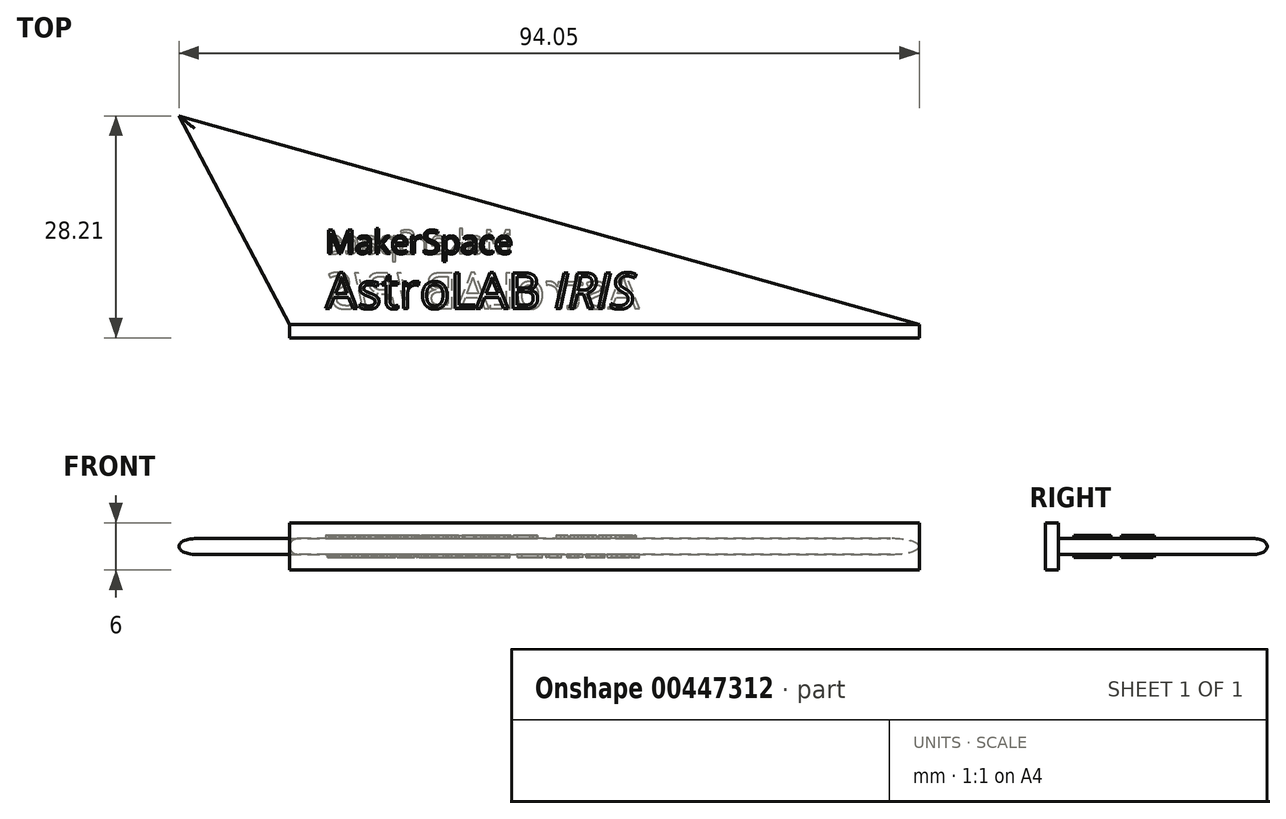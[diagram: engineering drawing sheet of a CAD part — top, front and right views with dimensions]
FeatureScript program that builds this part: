
annotation { "Feature Type Name" : "Feature", "Feature Type Description" : "" }
export const myFeature = defineFeature(function(context is Context, id is Id, definition is map)
    precondition{}
    {
        {
            var Q0;
            Q0=qCreatedBy(makeId("Front.planeOp"),FACE);
            var sketch = newSketch(context, id + "F0", { "sketchPlane" : qUnion([Q0])});
            skLineSegment(sketch, "E0.bottom", {"start": v(-40, 3) * mm, "end": v(40, 3) * mm});
            skLineSegment(sketch, "E0.top", {"start": v(-40, -3) * mm, "end": v(40, -3) * mm});
            skLineSegment(sketch, "E0.left", {"start": v(-40, 3) * mm, "end": v(-40, -3) * mm});
            skLineSegment(sketch, "E0.right", {"start": v(40, 3) * mm, "end": v(40, -3) * mm});
            skPoint(sketch, "E0.middle", {"position": v(0, 0) * mm});
            skSolve(sketch);
        }
        {
            var Q0;
            Q0=qCreatedBy(makeId("Front.planeOp"),FACE);
            var sketch = newSketch(context, id + "F1", { "sketchPlane" : qUnion([Q0])});
            skLineSegment(sketch, "E1.bottom", {"start": v(-40, 0.85) * mm, "end": v(40, 0.85) * mm});
            skLineSegment(sketch, "E1.top", {"start": v(-40, -0.85) * mm, "end": v(40, -0.85) * mm});
            skLineSegment(sketch, "E1.left", {"start": v(-40, 0.85) * mm, "end": v(-40, -0.85) * mm});
            skLineSegment(sketch, "E1.right", {"start": v(40, 0.85) * mm, "end": v(40, -0.85) * mm});
            skPoint(sketch, "E1.middle", {"position": v(0, 0) * mm});
            skSolve(sketch);
        }
        {
            var Q0;
            Q0=qCreatedBy(makeId("Top.planeOp"),FACE);
            var sketch = newSketch(context, id + "F2", { "sketchPlane" : qUnion([Q0])});
            skLineSegment(sketch, "E2", {"start": v(40, 0) * mm, "end": v(-40, 0) * mm});
            skLineSegment(sketch, "E3", {"start": v(-40, 0) * mm, "end": v(-40, 26.5) * mm, "construction": true});
            skLineSegment(sketch, "E4", {"start": v(-40, 26.5) * mm, "end": v(-54.05, 26.5) * mm, "construction": true});
            skLineSegment(sketch, "E5", {"start": v(-54.05, 26.5) * mm, "end": v(-40, 0) * mm});
            skLineSegment(sketch, "E6", {"start": v(-54.05, 26.5) * mm, "end": v(40, 0) * mm});
            skSolve(sketch);
        }
        {
            var Q0;
            Q0 = qSketchRegion(id + "F0", true);
            extrude(context, id + "F3", {"entities" : qUnion([Q0]), "depth" : 1.7 * mm});
        }
        {
            var Q0;
            Q0=makeQuery(id+"F2.imprint","IMPRINT",FACE,{"disambiguationData":[TD([[makeQuery(id+"F2.imprint","IMPRINT",EDGE,{"derivedFrom":sQuery(id+"F2.wireOp",EDGE,"E2")}),-1.0]])]});
            extrude(context, id + "F4", {"entities" : qUnion([Q0]), "operationType" : NewBodyOperationType.ADD, "depth" : 2 * mm, "symmetric" : true});
        }
        {
            var Q0;
            Q0=makeQuery(id+"F4.opExtrude","CAP_EDGE",EDGE,{"disambiguationData":[OSD([sQuery(id+"F2.wireOp",EDGE,"E6")])],"isStart":false});
            var Q1;
            Q1=makeQuery(id+"F4.opExtrude","CAP_EDGE",EDGE,{"disambiguationData":[OSD([sQuery(id+"F2.wireOp",EDGE,"E6")])],"isStart":true});
            var Q2;
            Q2=makeQuery(id+"F4.opExtrude","CAP_EDGE",EDGE,{"disambiguationData":[OSD([sQuery(id+"F2.wireOp",EDGE,"E5")])],"isStart":false});
            var Q3;
            Q3=makeQuery(id+"F4.opExtrude","CAP_EDGE",EDGE,{"disambiguationData":[OSD([sQuery(id+"F2.wireOp",EDGE,"E5")])],"isStart":true});
            fillet(context, id + "F5", {"entities" : qUnion([Q0, Q1, Q2, Q3]), "radius" : 1 * mm, "tangentPropagation" : true, "allowEdgeOverflow" : false});
        }
        {
            var Q0;
            Q0=makeQuery(id+"F4.opExtrude","CAP_FACE",FACE,{"disambiguationData":[OSD([sQuery(id+"F2.wireOp",EDGE,"E2"),sQuery(id+"F2.wireOp",EDGE,"E5"),sQuery(id+"F2.wireOp",EDGE,"E6")])],"isStart":false});
            var sketch = newSketch(context, id + "F6", { "sketchPlane" : qUnion([Q0])});
            skText(sketch, "E7", { "text": "MakerSpace", "fontName": "OpenSans-Regular.ttf"});
            skLineSegment(sketch, "E8", {"start": v(-35.43, 2) * mm, "end": v(-35.43, 12) * mm, "construction": true});
            skLineSegment(sketch, "E9", {"start": v(-35.43, 2) * mm, "end": v(-35.43, 0) * mm, "construction": true});
            skLineSegment(sketch, "E10", {"start": v(-35.43, 2) * mm, "end": v(-39.93, 2) * mm, "construction": true});
            skText(sketch, "E11", { "text": "AstroLAB ", "fontName": "OpenSans-Regular.ttf"});
            skText(sketch, "E12", { "text": " IRIS", "fontName": "OpenSans-Italic.ttf"});
            const initialGuessF6  = {"E7": [-0.03543, 0.009, 1, 0, 0.003], "E11": [-0.03543, 0.002, 1, 0, 0.0046], "E12": [-0.00805, 0.002, 1, 0, 0.0046]};
            skSetInitialGuess(sketch, initialGuessF6);
            skSolve(sketch);
        }
        {
            var Q0;
            Q0=makeQuery(id+"F4.opExtrude","CAP_FACE",FACE,{"disambiguationData":[OSD([sQuery(id+"F2.wireOp",EDGE,"E2"),sQuery(id+"F2.wireOp",EDGE,"E5"),sQuery(id+"F2.wireOp",EDGE,"E6")])],"isStart":true});
            var sketch = newSketch(context, id + "F7", { "sketchPlane" : qUnion([Q0])});
            skLineSegment(sketch, "E13", {"start": v(-35.43, 0) * mm, "end": v(-35.43, -2) * mm, "construction": true});
            skLineSegment(sketch, "E14", {"start": v(-35.43, -2) * mm, "end": v(-39.93, -2) * mm, "construction": true});
            skLineSegment(sketch, "E15", {"start": v(-35.43, -2) * mm, "end": v(-35.43, -12) * mm, "construction": true});
            skText(sketch, "E16", { "text": "MakerSpace", "fontName": "OpenSans-Regular.ttf"});
            skText(sketch, "E17", { "text": " IRIS", "fontName": "OpenSans-Italic.ttf"});
            skText(sketch, "E18", { "text": "AstroLAB", "fontName": "OpenSans-Regular.ttf"});
            const initialGuessF7  = {"E16": [-0.0116, -0.009, -1, 0, 0.003], "E17": [-0.02293, -0.002, -1, 0, 0.0046], "E18": [0.00445, -0.002, -1, 0, 0.0046]};
            skSetInitialGuess(sketch, initialGuessF7);
            skSolve(sketch);
        }
        {
            var Q0;
            Q0 = qSketchRegion(id + "F7", true);
            extrude(context, id + "F8", {"entities" : qUnion([Q0]), "operationType" : NewBodyOperationType.ADD, "depth" : 0.4 * mm});
        }
        {
            var Q0;
            Q0 = qSketchRegion(id + "F6", true);
            extrude(context, id + "F9", {"entities" : qUnion([Q0]), "operationType" : NewBodyOperationType.ADD, "depth" : .4 * mm});
        }
    });
